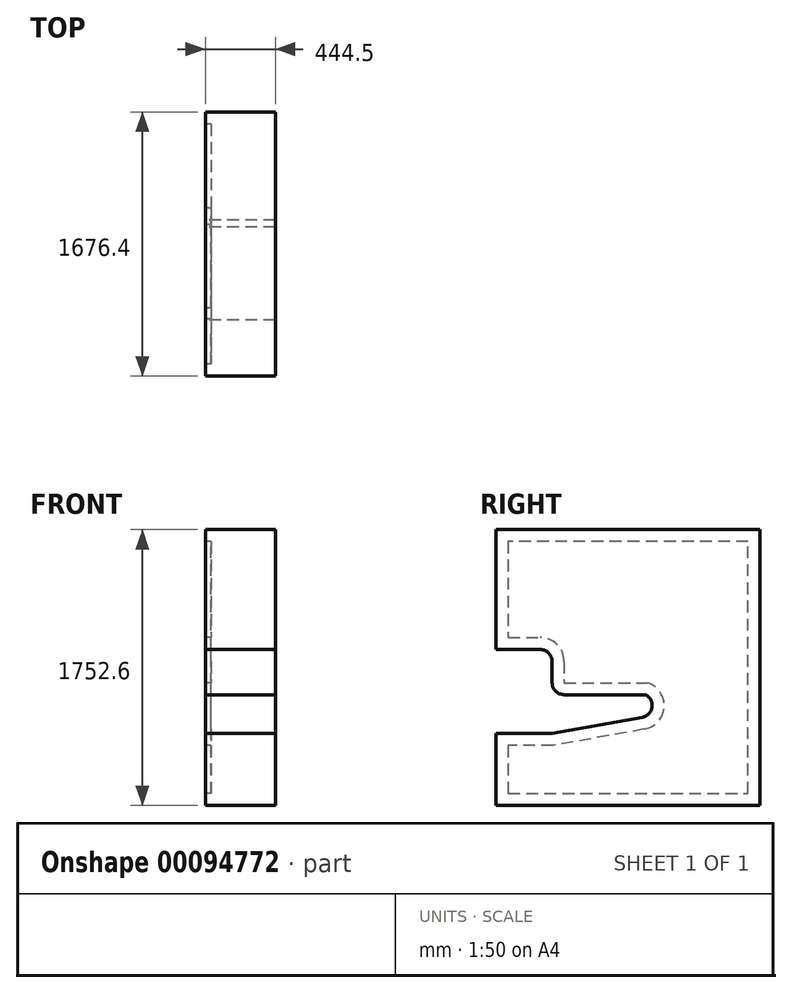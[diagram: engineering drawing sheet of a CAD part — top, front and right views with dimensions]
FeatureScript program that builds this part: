
annotation { "Feature Type Name" : "Feature", "Feature Type Description" : "" }
export const myFeature = defineFeature(function(context is Context, id is Id, definition is map)
    precondition{}
    {
        {
            var Q0;
            Q0=qCreatedBy(makeId("Right.planeOp"),FACE);
            var sketch = newSketch(context, id + "F0", { "sketchPlane" : qUnion([Q0])});
            skLineSegment(sketch, "E0", {"start": v(-914.4, 0) * mm, "end": v(762, 0) * mm, "construction": true});
            skLineSegment(sketch, "E1.0", {"start": v(-914.4, 457.2) * mm, "end": v(0, 457.2) * mm, "construction": true});
            skLineSegment(sketch, "E2.0", {"start": v(-1354.22, 635) * mm, "end": v(1358.95, 635) * mm, "construction": true});
            skLineSegment(sketch, "E3.0", {"start": v(-914.4, 990.6) * mm, "end": v(0, 990.6) * mm, "construction": true});
            skLineSegment(sketch, "E4.0", {"start": v(-914.4, 1295.4) * mm, "end": v(0, 1295.4) * mm, "construction": true});
            skLineSegment(sketch, "E5", {"start": v(-914.4, 1295.4) * mm, "end": v(-914.4, 0) * mm, "construction": true});
            skLineSegment(sketch, "E6.0", {"start": v(-558.8, 1295.4) * mm, "end": v(-558.8, 0) * mm, "construction": true});
            skLineSegment(sketch, "E7.0", {"start": v(-1354.22, 1752.6) * mm, "end": v(1358.95, 1752.6) * mm, "construction": true});
            skLineSegment(sketch, "E8", {"start": v(0, -258.78) * mm, "end": v(0, 1895.33) * mm, "construction": true});
            skLineSegment(sketch, "E9.0", {"start": v(762, -258.78) * mm, "end": v(762, 1895.33) * mm, "construction": true});
            skArc(sketch, "E10", {"start": v(13.47, 560) * mm, "mid": v(75.49, 624.6) * mm, "end": v(33.24, 703.57) * mm});
            skLineSegment(sketch, "E11", {"start": v(-558.8, 457.2) * mm, "end": v(13.47, 560) * mm});
            skLineSegment(sketch, "E12", {"start": v(-635, 990.6) * mm, "end": v(-914.4, 990.6) * mm});
            skLineSegment(sketch, "E13", {"start": v(-914.4, 990.6) * mm, "end": v(-914.4, 1295.4) * mm});
            skLineSegment(sketch, "E14", {"start": v(0, 1752.6) * mm, "end": v(762, 1752.6) * mm});
            skLineSegment(sketch, "E15", {"start": v(762, 1752.6) * mm, "end": v(762, 0) * mm});
            skLineSegment(sketch, "E16", {"start": v(-914.4, 0) * mm, "end": v(762, 0) * mm});
            skLineSegment(sketch, "E17", {"start": v(-914.4, 0) * mm, "end": v(-914.4, 457.2) * mm});
            skLineSegment(sketch, "E18", {"start": v(-914.4, 457.2) * mm, "end": v(-558.8, 457.2) * mm});
            skPoint(sketch, "E19.orphan", {"position": v(0, 557.58) * mm});
            skLineSegment(sketch, "E20", {"start": v(33.24, 703.57) * mm, "end": v(-482.6, 703.57) * mm});
            skLineSegment(sketch, "E21", {"start": v(-558.8, 779.77) * mm, "end": v(-558.8, 914.4) * mm});
            skPoint(sketch, "E22.visualSharp", {"position": v(-558.8, 703.57) * mm});
            skArc(sketch, "E22.filletArc", {"start": v(-558.8, 779.77) * mm, "mid": v(-536.48, 725.89) * mm, "end": v(-482.6, 703.57) * mm});
            skPoint(sketch, "E23.visualSharp", {"position": v(-558.8, 990.6) * mm});
            skArc(sketch, "E23.filletArc", {"start": v(-558.8, 914.4) * mm, "mid": v(-581.12, 968.28) * mm, "end": v(-635, 990.6) * mm});
            skLineSegment(sketch, "E24", {"start": v(-914.4, 1295.4) * mm, "end": v(-914.4, 1752.6) * mm});
            skLineSegment(sketch, "E25", {"start": v(-914.4, 1752.6) * mm, "end": v(0, 1752.6) * mm});
            skSolve(sketch);
        }
        {
            var Q0;
            Q0=qSketchRegion(id+"F0",true);
            extrude(context, id + "F1", {"entities" : qUnion([Q0]), "endBound" : BoundingType.SYMMETRIC, "depth" : 76.2 * mm});
        }
        {
            var Q0;
            Q0=qCreatedBy(makeId("Right.planeOp"),FACE);
            var sketch = newSketch(context, id + "F2", { "sketchPlane" : qUnion([Q0])});
            skArc(sketch, "E26.0.0", {"start": v(33.24, 703.57) * mm, "mid": v(75.49, 624.6) * mm, "end": v(13.47, 560) * mm});
            skLineSegment(sketch, "E26.0.1", {"start": v(13.47, 560) * mm, "end": v(-558.8, 457.2) * mm});
            skLineSegment(sketch, "E26.0.2", {"start": v(-558.8, 457.2) * mm, "end": v(-914.4, 457.2) * mm});
            skLineSegment(sketch, "E26.0.3", {"start": v(-914.4, 457.2) * mm, "end": v(-914.4, 0) * mm});
            skLineSegment(sketch, "E26.0.4", {"start": v(-914.4, 0) * mm, "end": v(762, 0) * mm});
            skLineSegment(sketch, "E26.0.5", {"start": v(762, 0) * mm, "end": v(762, 1752.6) * mm});
            skLineSegment(sketch, "E26.0.6", {"start": v(762, 1752.6) * mm, "end": v(-914.4, 1752.6) * mm});
            skLineSegment(sketch, "E26.0.7", {"start": v(-914.4, 1752.6) * mm, "end": v(-914.4, 990.6) * mm});
            skLineSegment(sketch, "E26.0.8", {"start": v(-914.4, 990.6) * mm, "end": v(-635, 990.6) * mm});
            skArc(sketch, "E26.0.9", {"start": v(-635, 990.6) * mm, "mid": v(-581.12, 968.28) * mm, "end": v(-558.8, 914.4) * mm});
            skLineSegment(sketch, "E26.0.10", {"start": v(-558.8, 914.4) * mm, "end": v(-558.8, 779.77) * mm});
            skArc(sketch, "E26.0.11", {"start": v(-558.8, 779.77) * mm, "mid": v(-536.48, 725.89) * mm, "end": v(-482.6, 703.57) * mm});
            skLineSegment(sketch, "E26.0.12", {"start": v(-482.6, 703.57) * mm, "end": v(33.24, 703.57) * mm});
            skLineSegment(sketch, "E27.0", {"start": v(685.8, 76.2) * mm, "end": v(685.8, 1676.4) * mm});
            skLineSegment(sketch, "E27.1", {"start": v(-838.2, 76.2) * mm, "end": v(685.8, 76.2) * mm});
            skLineSegment(sketch, "E27.2", {"start": v(-482.6, 914.4) * mm, "end": v(-482.6, 779.77) * mm});
            skArc(sketch, "E27.3", {"start": v(-635, 1066.8) * mm, "mid": v(-527.24, 1022.16) * mm, "end": v(-482.6, 914.4) * mm});
            skLineSegment(sketch, "E27.4", {"start": v(-838.2, 1066.8) * mm, "end": v(-635, 1066.8) * mm});
            skLineSegment(sketch, "E27.5", {"start": v(-838.2, 1676.4) * mm, "end": v(-838.2, 1066.8) * mm});
            skLineSegment(sketch, "E27.6", {"start": v(-482.6, 779.77) * mm, "end": v(-482.6, 779.77) * mm});
            skLineSegment(sketch, "E27.7", {"start": v(-482.6, 779.77) * mm, "end": v(47.63, 779.77) * mm});
            skLineSegment(sketch, "E27.8", {"start": v(685.8, 1676.4) * mm, "end": v(-838.2, 1676.4) * mm});
            skArc(sketch, "E27.9", {"start": v(47.63, 779.77) * mm, "mid": v(152.03, 624.33) * mm, "end": v(26.95, 485) * mm});
            skLineSegment(sketch, "E27.10", {"start": v(26.95, 485) * mm, "end": v(-552.01, 381) * mm});
            skLineSegment(sketch, "E27.11", {"start": v(-552.01, 381) * mm, "end": v(-838.2, 381) * mm});
            skLineSegment(sketch, "E27.12", {"start": v(-838.2, 381) * mm, "end": v(-838.2, 76.2) * mm});
            skSolve(sketch);
        }
        {
            var Q0;
            Q0=qSketchRegion(id+"F2",true);
            var Q1;
            Q1=makeQuery(id+"F1.opExtrude","CAP_FACE",FACE,{"disambiguationData":[OSD([sQuery(id+"F0.wireOp",EDGE,"E10"),sQuery(id+"F0.wireOp",EDGE,"E11"),sQuery(id+"F0.wireOp",EDGE,"E12"),sQuery(id+"F0.wireOp",EDGE,"E13"),sQuery(id+"F0.wireOp",EDGE,"E14"),sQuery(id+"F0.wireOp",EDGE,"E15"),sQuery(id+"F0.wireOp",EDGE,"E16"),sQuery(id+"F0.wireOp",EDGE,"E17"),sQuery(id+"F0.wireOp",EDGE,"E18"),sQuery(id+"F0.wireOp",EDGE,"E20"),sQuery(id+"F0.wireOp",EDGE,"E21"),sQuery(id+"F0.wireOp",EDGE,"E22.filletArc"),sQuery(id+"F0.wireOp",EDGE,"E23.filletArc"),sQuery(id+"F0.wireOp",EDGE,"E24"),sQuery(id+"F0.wireOp",EDGE,"E25")])],"isStart":false});
            extrude(context, id + "F3", {"entities" : qUnion([Q0, Q1]), "endBound" : BoundingType.SYMMETRIC, "depth" : 406.4 * mm});
        }
        {
            var Q0;
            Q0=makeQuery(id+"F1.opExtrude","SWEPT_BODY",BODY,{"disambiguationData":[OSD([sQuery(id+"F0.wireOp",EDGE,"E10"),sQuery(id+"F0.wireOp",EDGE,"E11"),sQuery(id+"F0.wireOp",EDGE,"E12"),sQuery(id+"F0.wireOp",EDGE,"E13"),sQuery(id+"F0.wireOp",EDGE,"E14"),sQuery(id+"F0.wireOp",EDGE,"E15"),sQuery(id+"F0.wireOp",EDGE,"E16"),sQuery(id+"F0.wireOp",EDGE,"E17"),sQuery(id+"F0.wireOp",EDGE,"E18"),sQuery(id+"F0.wireOp",EDGE,"E20"),sQuery(id+"F0.wireOp",EDGE,"E21"),sQuery(id+"F0.wireOp",EDGE,"E22.filletArc"),sQuery(id+"F0.wireOp",EDGE,"E23.filletArc"),sQuery(id+"F0.wireOp",EDGE,"E24"),sQuery(id+"F0.wireOp",EDGE,"E25")])]});
            var Q1;
            Q1=makeQuery(id+"F3.opExtrude","SWEPT_BODY",BODY,{"disambiguationData":[OSD([sQuery(id+"F2.wireOp",EDGE,"E26.0.0"),sQuery(id+"F2.wireOp",EDGE,"E26.0.1"),sQuery(id+"F2.wireOp",EDGE,"E26.0.2"),sQuery(id+"F2.wireOp",EDGE,"E26.0.3"),sQuery(id+"F2.wireOp",EDGE,"E26.0.4"),sQuery(id+"F2.wireOp",EDGE,"E26.0.5"),sQuery(id+"F2.wireOp",EDGE,"E26.0.6"),sQuery(id+"F2.wireOp",EDGE,"E26.0.7"),sQuery(id+"F2.wireOp",EDGE,"E26.0.8"),sQuery(id+"F2.wireOp",EDGE,"E26.0.9"),sQuery(id+"F2.wireOp",EDGE,"E26.0.10"),sQuery(id+"F2.wireOp",EDGE,"E26.0.11"),sQuery(id+"F2.wireOp",EDGE,"E26.0.12"),sQuery(id+"F2.wireOp",EDGE,"E27.0"),sQuery(id+"F2.wireOp",EDGE,"E27.1"),sQuery(id+"F2.wireOp",EDGE,"E27.2"),sQuery(id+"F2.wireOp",EDGE,"E27.3"),sQuery(id+"F2.wireOp",EDGE,"E27.4"),sQuery(id+"F2.wireOp",EDGE,"E27.5"),sQuery(id+"F2.wireOp",EDGE,"E27.7"),sQuery(id+"F2.wireOp",EDGE,"E27.8"),sQuery(id+"F2.wireOp",EDGE,"E27.9"),sQuery(id+"F2.wireOp",EDGE,"E27.10"),sQuery(id+"F2.wireOp",EDGE,"E27.11"),sQuery(id+"F2.wireOp",EDGE,"E27.12")])]});
            var Q2;
            Q2=makeQuery(id+"F3.opExtrude","SWEPT_BODY",BODY,{"disambiguationData":[OSD([sQuery(id+"F0.wireOp",EDGE,"E10"),sQuery(id+"F0.wireOp",EDGE,"E11"),sQuery(id+"F0.wireOp",EDGE,"E12"),sQuery(id+"F0.wireOp",EDGE,"E13"),sQuery(id+"F0.wireOp",EDGE,"E14"),sQuery(id+"F0.wireOp",EDGE,"E15"),sQuery(id+"F0.wireOp",EDGE,"E16"),sQuery(id+"F0.wireOp",EDGE,"E17"),sQuery(id+"F0.wireOp",EDGE,"E18"),sQuery(id+"F0.wireOp",EDGE,"E20"),sQuery(id+"F0.wireOp",EDGE,"E21"),sQuery(id+"F0.wireOp",EDGE,"E22.filletArc"),sQuery(id+"F0.wireOp",EDGE,"E23.filletArc"),sQuery(id+"F0.wireOp",EDGE,"E24"),sQuery(id+"F0.wireOp",EDGE,"E25")])]});
            booleanBodies(context, id + "F4", {"operationType" : BooleanOperationType.UNION, "tools" : qUnion([Q0, Q1, Q2])});
        }
    });
